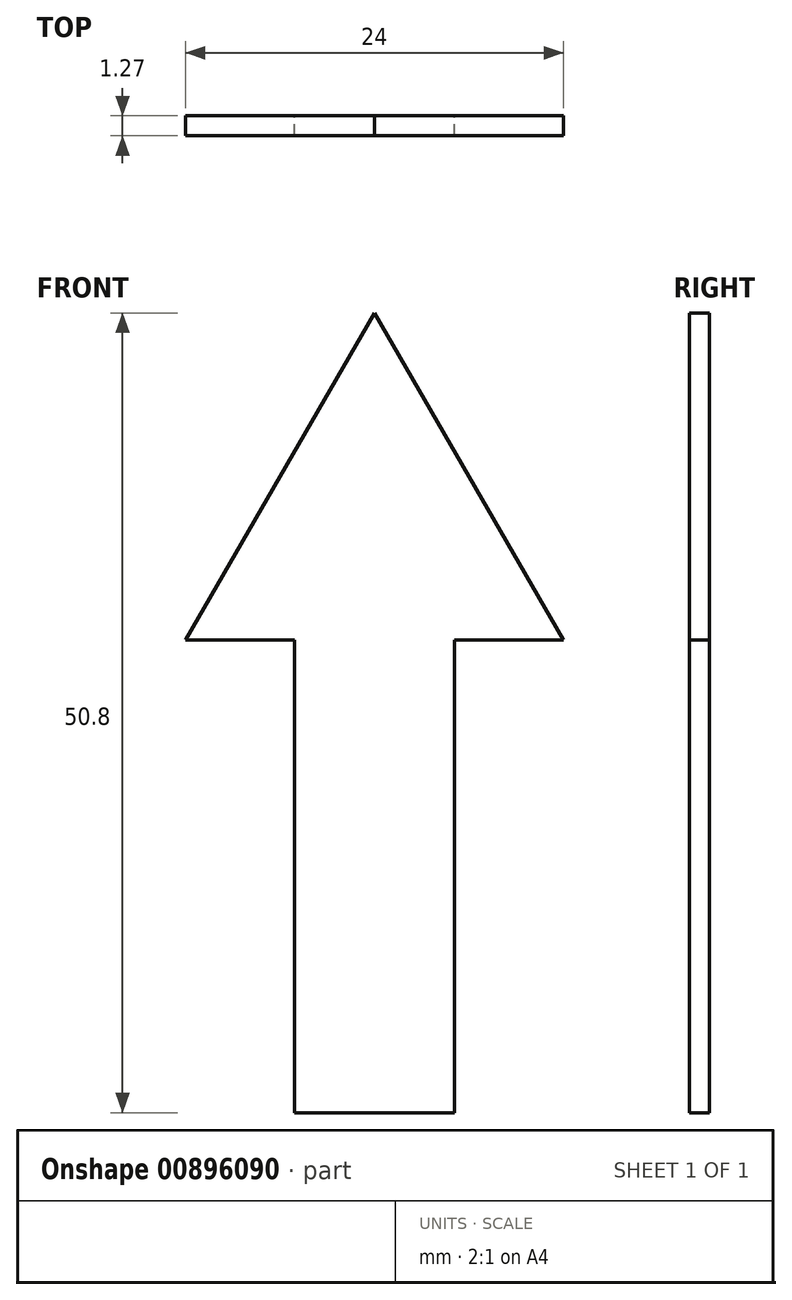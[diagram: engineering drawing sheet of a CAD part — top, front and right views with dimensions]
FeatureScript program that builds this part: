
annotation { "Feature Type Name" : "Feature", "Feature Type Description" : "" }
export const myFeature = defineFeature(function(context is Context, id is Id, definition is map)
    precondition{}
    {
        {
            var Q0;
            Q0=qCreatedBy(makeId("Front.planeOp"),FACE);
            var sketch = newSketch(context, id + "F0", { "sketchPlane" : qUnion([Q0])});
            skLineSegment(sketch, "E0", {"start": v(-93.86, -7.5) * mm, "end": v(-83.7, -7.5) * mm});
            skLineSegment(sketch, "E1", {"start": v(-83.7, -7.5) * mm, "end": v(-83.7, 22.52) * mm});
            skLineSegment(sketch, "E2", {"start": v(-83.7, 22.52) * mm, "end": v(-76.78, 22.52) * mm});
            skLineSegment(sketch, "E3", {"start": v(-76.78, 22.52) * mm, "end": v(-88.78, 43.3) * mm});
            skLineSegment(sketch, "E4", {"start": v(-88.78, 43.3) * mm, "end": v(-100.78, 22.52) * mm});
            skLineSegment(sketch, "E5", {"start": v(-100.78, 22.52) * mm, "end": v(-93.86, 22.52) * mm});
            skLineSegment(sketch, "E6", {"start": v(-93.86, 22.52) * mm, "end": v(-93.86, -7.5) * mm});
            skSolve(sketch);
        }
        {
            var Q0;
            Q0 = qSketchRegion(id + "F0", true);
            extrude(context, id + "F1", {"entities" : qUnion([Q0]), "depth" : 1.27 * mm, "offsetDistance" : 25.4 * mm});
        }
    });
